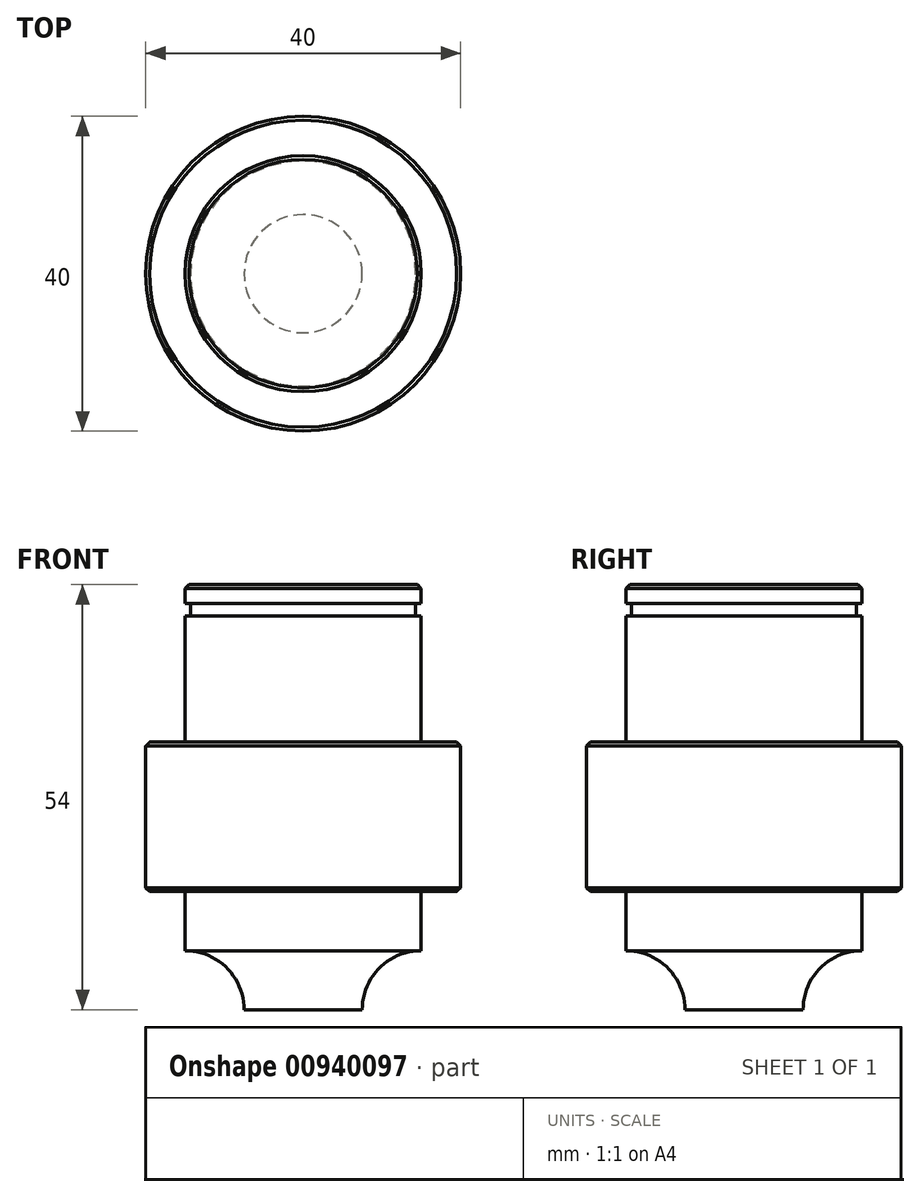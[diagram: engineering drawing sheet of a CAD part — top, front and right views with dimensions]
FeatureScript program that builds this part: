
annotation { "Feature Type Name" : "Feature", "Feature Type Description" : "" }
export const myFeature = defineFeature(function(context is Context, id is Id, definition is map)
    precondition{}
    {
        {
            var Q0;
            Q0=qCreatedBy(makeId("Front.planeOp"),FACE);
            var sketch = newSketch(context, id + "F0", { "sketchPlane" : qUnion([Q0])});
            skLineSegment(sketch, "E0", {"start": v(0, 54) * mm, "end": v(15, 54) * mm});
            skLineSegment(sketch, "E1", {"start": v(15, 54) * mm, "end": v(15, 51.6) * mm});
            skLineSegment(sketch, "E2", {"start": v(15, 51.6) * mm, "end": v(14.3, 51.6) * mm});
            skLineSegment(sketch, "E3", {"start": v(14.3, 51.6) * mm, "end": v(14.3, 50) * mm});
            skLineSegment(sketch, "E4", {"start": v(14.3, 50) * mm, "end": v(15, 50) * mm});
            skLineSegment(sketch, "E5", {"start": v(15, 50) * mm, "end": v(15, 34) * mm});
            skLineSegment(sketch, "E6", {"start": v(15, 34) * mm, "end": v(20, 34) * mm});
            skLineSegment(sketch, "E7", {"start": v(20, 34) * mm, "end": v(20, 15) * mm});
            skLineSegment(sketch, "E8", {"start": v(20, 15) * mm, "end": v(15, 15) * mm});
            skLineSegment(sketch, "E9", {"start": v(15, 15) * mm, "end": v(15, 7.5) * mm});
            skArc(sketch, "E10", {"start": v(15, 7.5) * mm, "mid": v(9.7, 5.3) * mm, "end": v(7.5, 0) * mm});
            skLineSegment(sketch, "E11", {"start": v(7.5, 0) * mm, "end": v(0, 0) * mm});
            skLineSegment(sketch, "E12", {"start": v(0, 0) * mm, "end": v(0, 54) * mm});
            skSolve(sketch);
        }
        {
            var Q0;
            Q0=makeQuery(id+"F0.imprint","IMPRINT",FACE,{"disambiguationData":[TD([[makeQuery(id+"F0.imprint","IMPRINT",EDGE,{"derivedFrom":sQuery(id+"F0.wireOp",EDGE,"E0")}),-1.0]])]});
            var Q1;
            Q1=sQuery(id+"F0.wireOp",EDGE,"E12");
            revolve(context, id + "F1", {"surfaceOperationType" : NewSurfaceOperationType.NEW, "entities" : qUnion([Q0]), "axis" : qUnion([Q1]), "revolveType" : RevolveType.FULL});
        }
        {
            var Q0;
            Q0=makeQuery(id+"F1.opRevolve","SWEPT_EDGE",EDGE,{"disambiguationData":[OSD([sQuery(id+"F0.wireOp",EDGE,"E0"),sQuery(id+"F0.wireOp",EDGE,"E1")])]});
            var Q1;
            Q1=makeQuery(id+"F1.opRevolve","SWEPT_EDGE",EDGE,{"disambiguationData":[OSD([sQuery(id+"F0.wireOp",EDGE,"E6"),sQuery(id+"F0.wireOp",EDGE,"E7")])]});
            var Q2;
            Q2=makeQuery(id+"F1.opRevolve","SWEPT_EDGE",EDGE,{"disambiguationData":[OSD([sQuery(id+"F0.wireOp",EDGE,"E7"),sQuery(id+"F0.wireOp",EDGE,"E8")])]});
            chamfer(context, id + "F2", {"entities" : qUnion([Q0, Q1, Q2]), "width" : 0.5 * mm, "tangentPropagation" : true});
        }
    });
